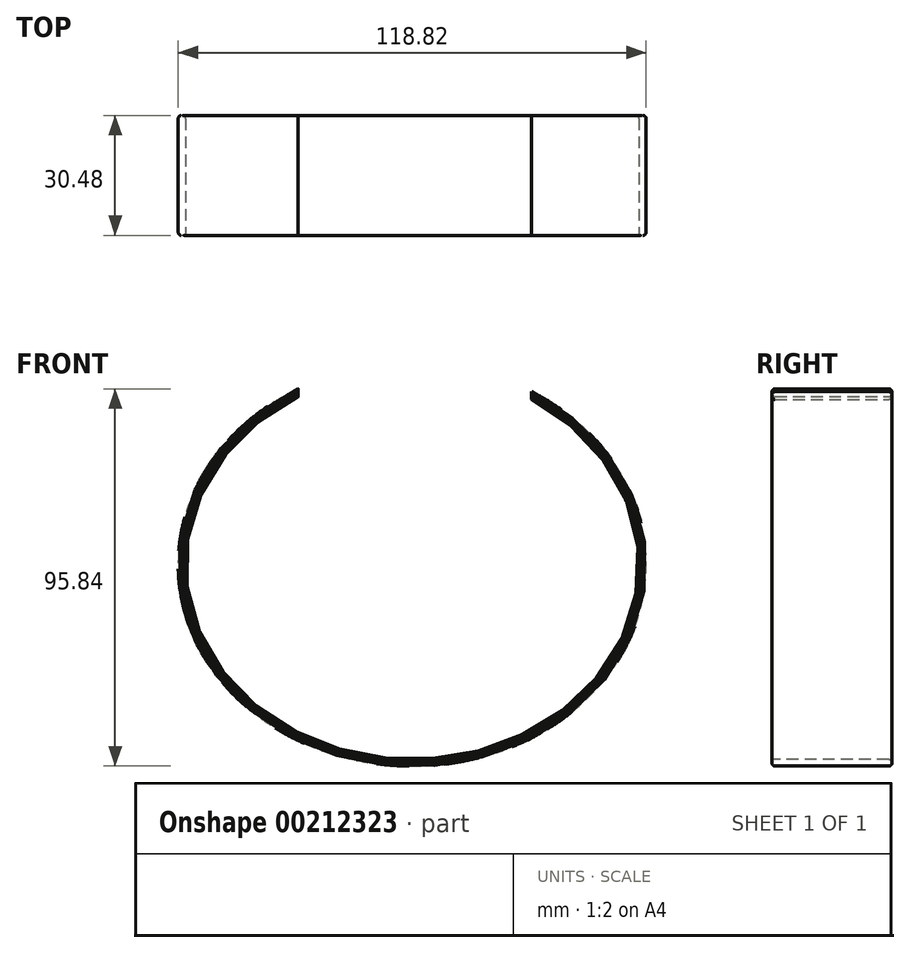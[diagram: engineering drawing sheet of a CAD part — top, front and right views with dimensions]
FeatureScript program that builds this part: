
annotation { "Feature Type Name" : "Feature", "Feature Type Description" : "" }
export const myFeature = defineFeature(function(context is Context, id is Id, definition is map)
    precondition{}
    {
        {
            var Q0;
            Q0=qCreatedBy(makeId("Front.planeOp"),FACE);
            var sketch = newSketch(context, id + "F0", { "sketchPlane" : qUnion([Q0])});
            skEllipticalArc(sketch, "E0", {});
            skEllipticalArc(sketch, "E1", {});
            skLineSegment(sketch, "E2", {"start": v(-28.94, 44.68) * mm, "end": v(-28.94, 42.7) * mm});
            skLineSegment(sketch, "E3", {"start": v(30.37, 43.97) * mm, "end": v(30.37, 41.96) * mm});
            skPoint(sketch, "E4.start.orphan", {"position": v(27.71, 43.3) * mm});
            skPoint(sketch, "E5.orphan", {"position": v(-27.71, 43.3) * mm});
            const initialGuessF0  = {"E0": [0, 0, 1, 0, 0.05941298900988619, 0.051156330804304005, 2.07959392078285, 1.0341692596797432], "E1": [0, 0, 1, 0, 0.057563309739760524, 0.04939995729614715, 2.0976085573953, 1.014943727104223]};
            skSetInitialGuess(sketch, initialGuessF0);
            skSolve(sketch);
        }
        {
            var Q0;
            Q0=makeQuery(id+"F0.imprint","IMPRINT",FACE,{"disambiguationData":[TD([[makeQuery(id+"F0.imprint","IMPRINT",EDGE,{"derivedFrom":sQuery(id+"F0.wireOp",EDGE,"E0")}),1.0]])]});
            extrude(context, id + "F1", {"entities" : qUnion([Q0]), "depth" : 30.48 * mm});
        }
        {
            var Q0;
            Q0=makeQuery(id+"F1.opExtrude","CAP_EDGE",EDGE,{"disambiguationData":[OSD([sQuery(id+"F0.wireOp",EDGE,"E1")])],"isStart":false});
            var Q1;
            Q1=makeQuery(id+"F1.opExtrude","CAP_EDGE",EDGE,{"disambiguationData":[OSD([sQuery(id+"F0.wireOp",EDGE,"E0")])],"isStart":false});
            var Q2;
            Q2=makeQuery(id+"F1.opExtrude","CAP_EDGE",EDGE,{"disambiguationData":[OSD([sQuery(id+"F0.wireOp",EDGE,"E1")])],"isStart":true});
            var Q3;
            Q3=makeQuery(id+"F1.opExtrude","CAP_EDGE",EDGE,{"disambiguationData":[OSD([sQuery(id+"F0.wireOp",EDGE,"E0")])],"isStart":true});
            fillet(context, id + "F2", {"entities" : qUnion([Q0, Q1, Q2, Q3]), "radius" : 0.76 * mm, "tangentPropagation" : true, "allowEdgeOverflow" : false});
        }
    });
